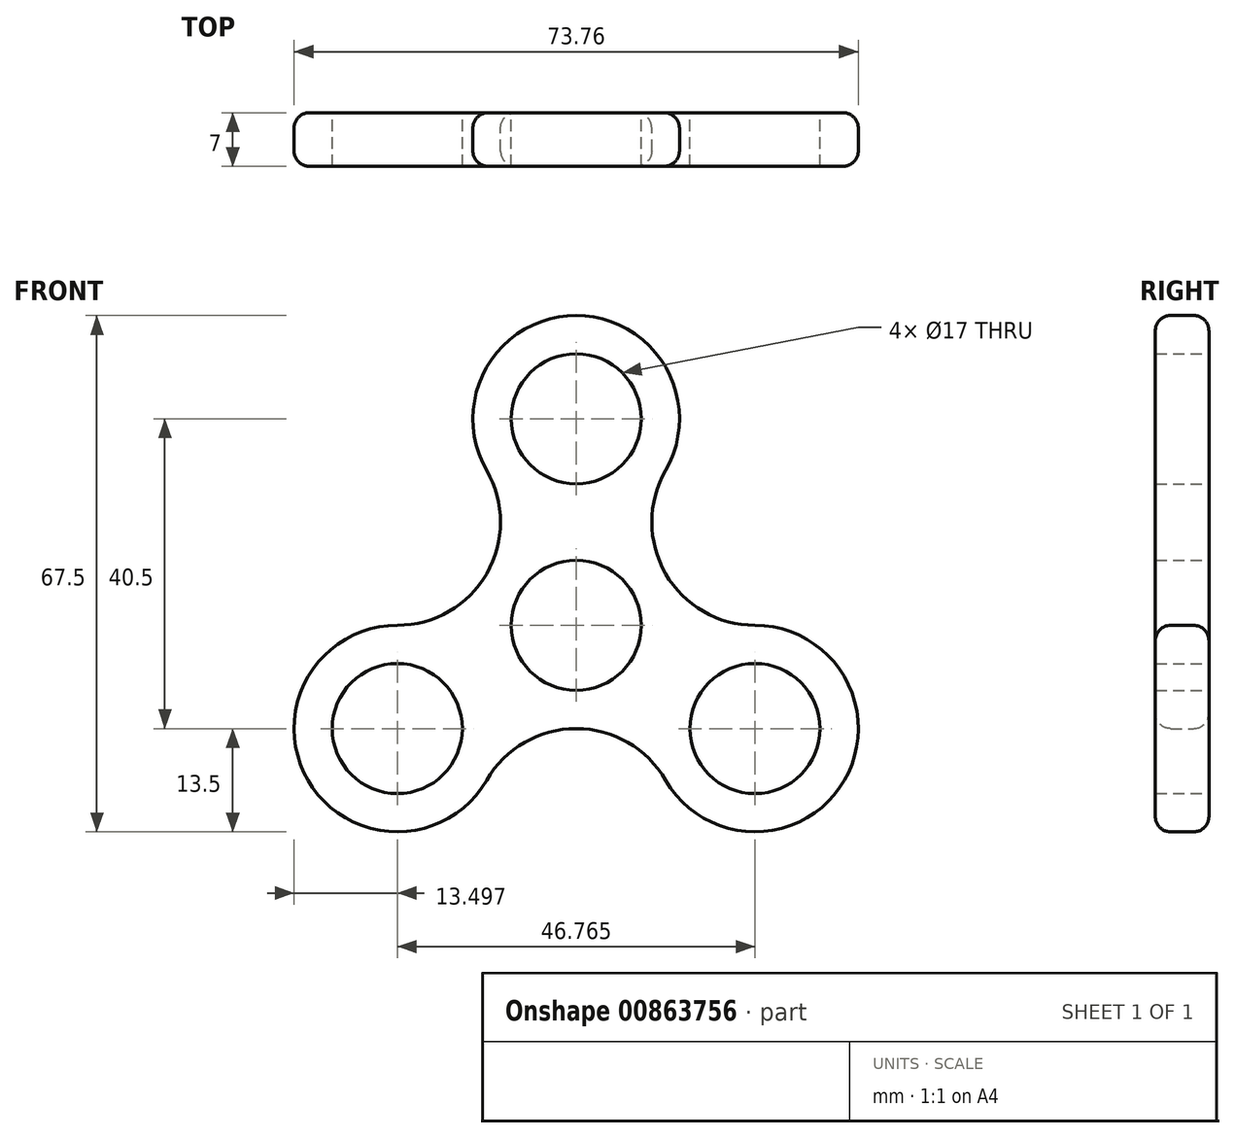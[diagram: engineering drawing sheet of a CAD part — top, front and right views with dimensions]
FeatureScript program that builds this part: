
annotation { "Feature Type Name" : "Feature", "Feature Type Description" : "" }
export const myFeature = defineFeature(function(context is Context, id is Id, definition is map)
    precondition{}
    {
        {
            var Q0;
            Q0=qCreatedBy(makeId("Front.planeOp"),FACE);
            var sketch = newSketch(context, id + "F0", { "sketchPlane" : qUnion([Q0])});
            skCircle(sketch, "E0", {"center": v(0, 0) * mm, "radius": 8.5 * mm});
            skCircle(sketch, "E1", {"center": v(0, 27) * mm, "radius": 8.5 * mm});
            skCircle(sketch, "E2.1.0", {"center": v(-23.38, -13.5) * mm, "radius": 8.5 * mm});
            skCircle(sketch, "E2.2.0", {"center": v(23.38, -13.5) * mm, "radius": 8.5 * mm});
            skArc(sketch, "E3", {"start": v(11.7, 20.25) * mm, "mid": v(0, 40.5) * mm, "end": v(-11.7, 20.25) * mm});
            skArc(sketch, "E4.1.0", {"start": v(-23.38, 0) * mm, "mid": v(-11.7, 6.75) * mm, "end": v(-11.7, 20.25) * mm});
            skArc(sketch, "E4.2.0", {"start": v(-23.38, 0) * mm, "mid": v(-35.07, -20.25) * mm, "end": v(-11.7, -20.25) * mm});
            skArc(sketch, "E4.3.0", {"start": v(11.7, -20.25) * mm, "mid": v(0, -13.5) * mm, "end": v(-11.7, -20.25) * mm});
            skArc(sketch, "E4.4.0", {"start": v(11.7, -20.25) * mm, "mid": v(35.07, -20.25) * mm, "end": v(23.38, 0) * mm});
            skArc(sketch, "E4.5.0", {"start": v(11.7, 20.25) * mm, "mid": v(11.7, 6.75) * mm, "end": v(23.38, 0) * mm});
            skSolve(sketch);
        }
        {
            var Q0;
            Q0=makeQuery(id+"F0.imprint","IMPRINT",FACE,{"disambiguationData":[TD([[makeQuery(id+"F0.imprint","IMPRINT",EDGE,{"derivedFrom":sQuery(id+"F0.wireOp",EDGE,"E0")}),-1.0]])]});
            extrude(context, id + "F1", {"entities" : qUnion([Q0]), "depth" : 7 * mm, "offsetDistance" : 25 * mm});
        }
        {
            var Q0;
            Q0=makeQuery(id+"F1.opExtrude","CAP_EDGE",EDGE,{"disambiguationData":[OSD([sQuery(id+"F0.wireOp",EDGE,"E4.2.0")])],"isStart":false});
            var Q1;
            Q1=makeQuery(id+"F1.opExtrude","CAP_EDGE",EDGE,{"disambiguationData":[OSD([sQuery(id+"F0.wireOp",EDGE,"E4.3.0")])],"isStart":false});
            var Q2;
            Q2=makeQuery(id+"F1.opExtrude","CAP_EDGE",EDGE,{"disambiguationData":[OSD([sQuery(id+"F0.wireOp",EDGE,"E4.4.0")])],"isStart":false});
            var Q3;
            Q3=makeQuery(id+"F1.opExtrude","CAP_EDGE",EDGE,{"disambiguationData":[OSD([sQuery(id+"F0.wireOp",EDGE,"E4.5.0")])],"isStart":false});
            var Q4;
            Q4=makeQuery(id+"F1.opExtrude","CAP_EDGE",EDGE,{"disambiguationData":[OSD([sQuery(id+"F0.wireOp",EDGE,"E3")])],"isStart":false});
            var Q5;
            Q5=makeQuery(id+"F1.opExtrude","CAP_EDGE",EDGE,{"disambiguationData":[OSD([sQuery(id+"F0.wireOp",EDGE,"E4.1.0")])],"isStart":false});
            fillet(context, id + "F2", {"entities" : qUnion([Q0, Q1, Q2, Q3, Q4, Q5]), "radius" : 2 * mm, "tangentPropagation" : true, "allowEdgeOverflow" : false});
        }
        {
            var Q0;
            Q0=makeQuery(id+"F1.opExtrude","CAP_EDGE",EDGE,{"disambiguationData":[OSD([sQuery(id+"F0.wireOp",EDGE,"E4.2.0")])],"isStart":true});
            var Q1;
            Q1=makeQuery(id+"F1.opExtrude","CAP_EDGE",EDGE,{"disambiguationData":[OSD([sQuery(id+"F0.wireOp",EDGE,"E4.3.0")])],"isStart":true});
            var Q2;
            Q2=makeQuery(id+"F1.opExtrude","CAP_EDGE",EDGE,{"disambiguationData":[OSD([sQuery(id+"F0.wireOp",EDGE,"E4.4.0")])],"isStart":true});
            fillet(context, id + "F3", {"entities" : qUnion([Q0, Q1, Q2]), "radius" : 2 * mm, "tangentPropagation" : true, "allowEdgeOverflow" : false});
        }
    });
